# Revit family: VCG-2_RFA
name_source: partatom
category: Aparatos sanitarios
units: mm (PartAtom-declared; Revit-internal decimal feet)

## family parameters
Activar corte en vistas = No
Compartido = No
Corte con vacíos al cargar = No
Cota de conector redondo = Usar diámetro
Mantener orientación de anotación = No
Número OmniClass = 23.45.00.00
Punto de cálculo de habitación = No
Se basa en plano de trabajo = No
Siempre vertical = Sí
Tipo de pieza = Normal
Título OmniClass = Sanitary, Laundry, and Cleaning Equipment

## types (1)
- VCG-2
    Chrome = Brass Chromed
    Comentarios de tipo = Llave para hospital
    Connection = ½" - 14 NPSM
    Descripción = Llave para hospital
    Elevación por defecto = 0"
    Fabricante = HELVEX
    Features = Llave de hospital con cuello de ganso giratorio manija corta. Cuello giratorio. Acabado Cromo. Presión mínima requerida 0.25 kg/ cm2
    Imagen de tipo = VCG-2.png
    Max. Working Pressure = 85.3 psi
    Min. Working Pressure = 2.8 psi
    Modelo = VCG-2
    Total Height = 15"
    Total Width = 2"
    URL = https://helvex.com.mx

## geometry (parser evidence)
native form markers: Sweep x3
no freeform markers — native parametric forms only
